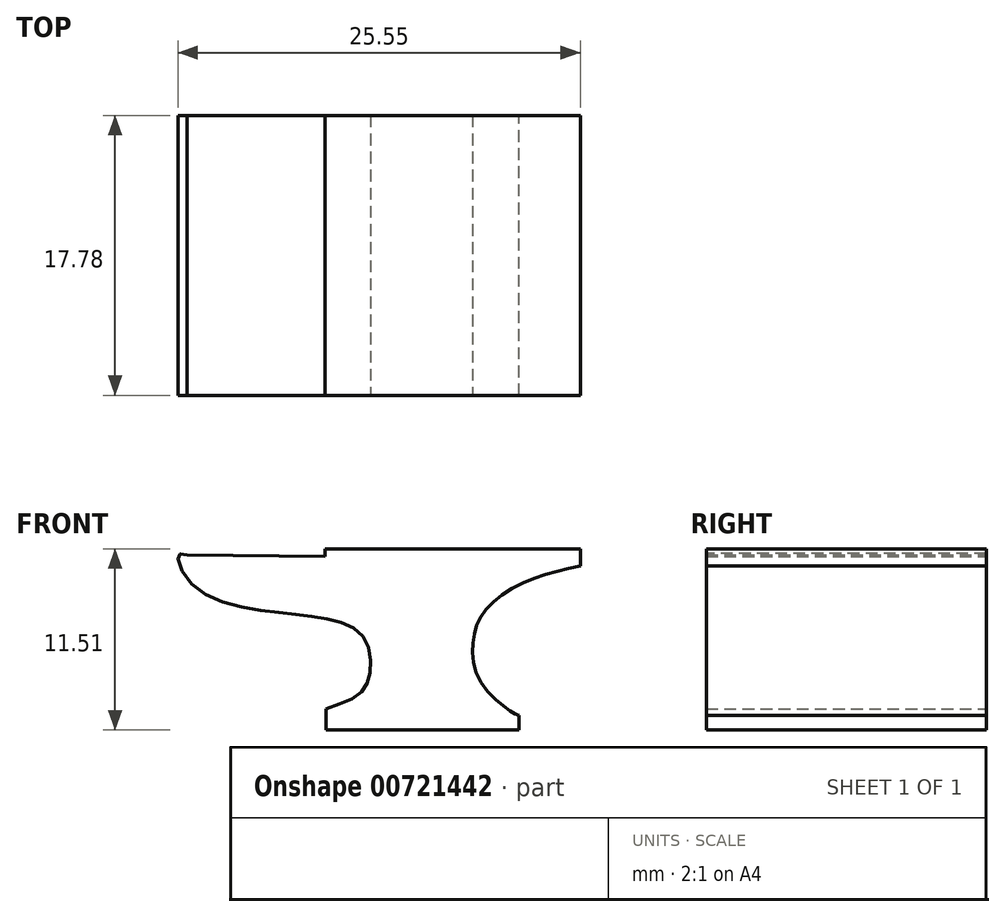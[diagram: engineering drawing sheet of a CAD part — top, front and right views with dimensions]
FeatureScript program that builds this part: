
annotation { "Feature Type Name" : "Feature", "Feature Type Description" : "" }
export const myFeature = defineFeature(function(context is Context, id is Id, definition is map)
    precondition{}
    {
        {
            var Q0;
            Q0=qCreatedBy(makeId("Front.planeOp"),FACE);
            var sketch = newSketch(context, id + "F0", { "sketchPlane" : qUnion([Q0])});
            skLineSegment(sketch, "E0", {"start": v(-3.31, -4.18) * mm, "end": v(12.9, -4.18) * mm});
            skLineSegment(sketch, "E1", {"start": v(12.9, -4.18) * mm, "end": v(12.9, -5.26) * mm});
            skLineSegment(sketch, "E2", {"start": v(-3.31, -4.18) * mm, "end": v(-3.31, -4.66) * mm});
            skFitSpline(sketch, "E3", {"points": [v(12.9, -5.26) * mm, v(9.4, -6.29) * mm, v(6.8, -8.18) * mm, v(6.1, -10.07) * mm, v(6.53, -12.56) * mm, v(8.42, -14.45) * mm, v(9.01, -14.77) * mm], "startDerivative": vector(-17.21, -3.76) * mm, "endDerivative": vector(5.56, -2.54) * mm});
            skLineSegment(sketch, "E4", {"start": v(9.01, -14.77) * mm, "end": v(9.01, -15.7) * mm});
            skLineSegment(sketch, "E5", {"start": v(9.01, -15.7) * mm, "end": v(-3.26, -15.7) * mm});
            skLineSegment(sketch, "E6", {"start": v(-3.26, -15.7) * mm, "end": v(-3.26, -14.34) * mm});
            skFitSpline(sketch, "E7", {"points": [v(-3.26, -14.34) * mm, v(-1.04, -13.31) * mm, v(-0.45, -11.85) * mm, v(-0.93, -9.7) * mm, v(-3.26, -8.61) * mm, v(-7.1, -8.12) * mm, v(-11.69, -6.5) * mm, v(-12.6, -4.56) * mm, v(-12.07, -4.56) * mm], "startDerivative": vector(20.35, 6.66) * mm, "endDerivative": vector(11.33, -3.14) * mm});
            skLineSegment(sketch, "E8", {"start": v(-12.07, -4.56) * mm, "end": v(-3.31, -4.66) * mm});
            skSolve(sketch);
        }
        {
            var Q0;
            Q0=makeQuery(id+"F0.imprint","IMPRINT",FACE,{"disambiguationData":[TD([[makeQuery(id+"F0.imprint","IMPRINT",EDGE,{"derivedFrom":sQuery(id+"F0.wireOp",EDGE,"E0")}),-1.0]])]});
            extrude(context, id + "F1", {"entities" : qUnion([Q0]), "depth" : 17.78 * mm, "offsetDistance" : 25.4 * mm});
        }
    });
